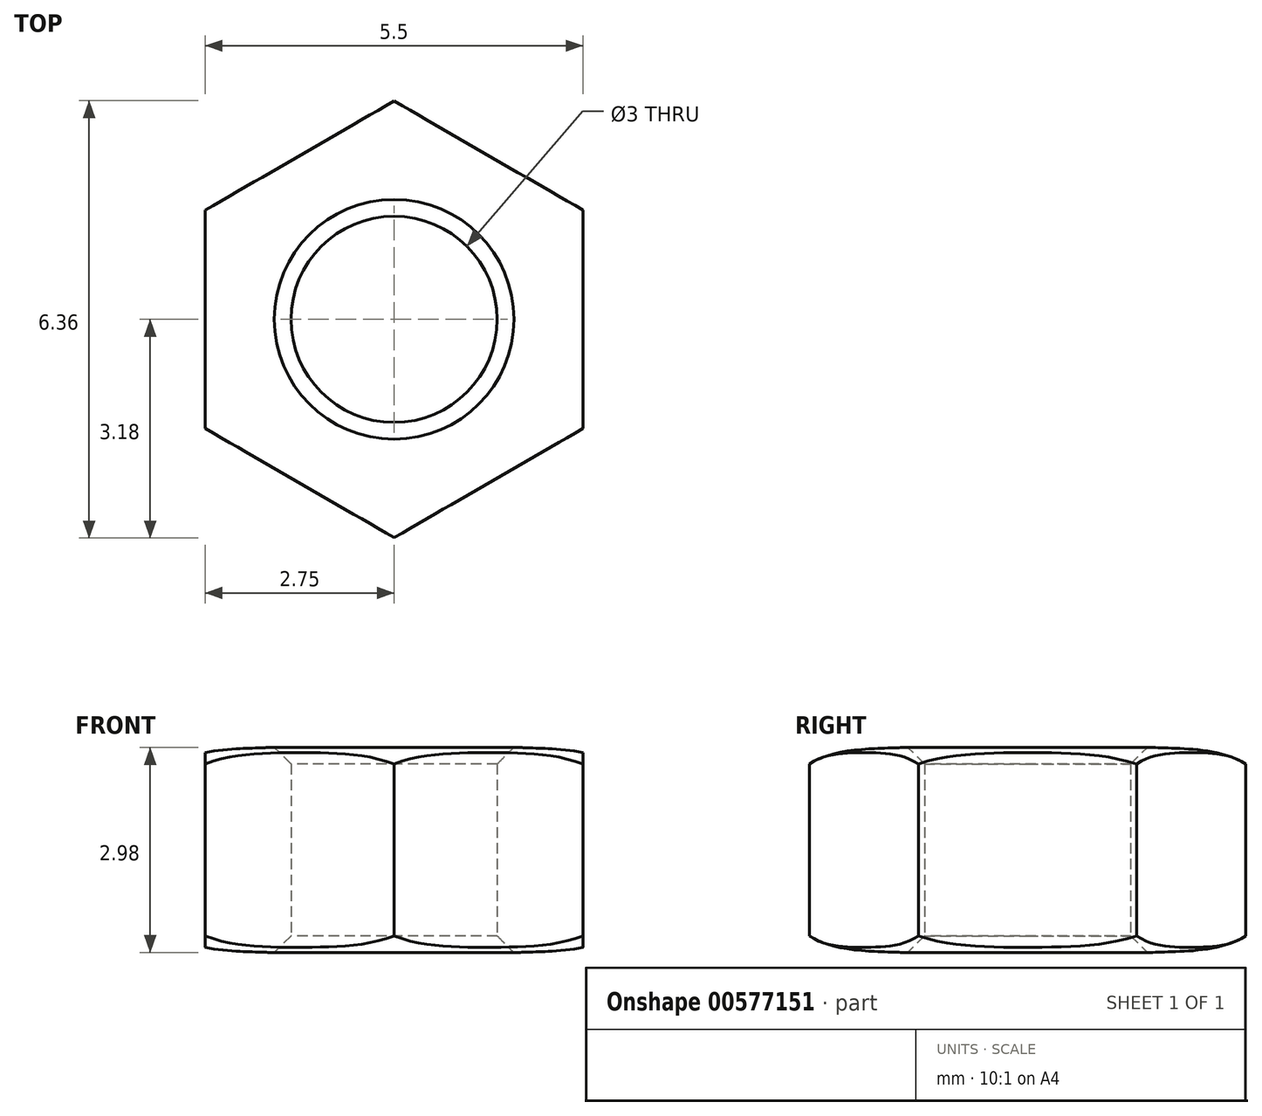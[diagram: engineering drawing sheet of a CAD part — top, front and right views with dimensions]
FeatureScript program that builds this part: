
annotation { "Feature Type Name" : "Feature", "Feature Type Description" : "" }
export const myFeature = defineFeature(function(context is Context, id is Id, definition is map)
    precondition{}
    {
        {
            var Q0;
            Q0=qCreatedBy(makeId("Top.planeOp"),FACE);
            var sketch = newSketch(context, id + "F0", { "sketchPlane" : qUnion([Q0])});
            skCircle(sketch, "E0.cCircle", {"center": v(0, 0) * mm, "radius": 2.75 * mm, "construction": true});
            skLineSegment(sketch, "E0.0", {"start": v(2.75, 1.59) * mm, "end": v(2.75, -1.59) * mm});
            skLineSegment(sketch, "E0.1", {"start": v(2.75, -1.59) * mm, "end": v(0, -3.18) * mm});
            skLineSegment(sketch, "E0.2", {"start": v(0, -3.18) * mm, "end": v(-2.75, -1.59) * mm});
            skLineSegment(sketch, "E0.3", {"start": v(-2.75, -1.59) * mm, "end": v(-2.75, 1.59) * mm});
            skLineSegment(sketch, "E0.4", {"start": v(-2.75, 1.59) * mm, "end": v(0, 3.18) * mm});
            skLineSegment(sketch, "E0.5", {"start": v(0, 3.18) * mm, "end": v(2.75, 1.59) * mm});
            skPoint(sketch, "E0.0.midPoint", {"position": v(2.75, 0) * mm});
            skCircle(sketch, "E1", {"center": v(0, 0) * mm, "radius": 1.5 * mm});
            skSolve(sketch);
        }
        {
            var Q0;
            Q0=qSketchRegion(id+"F0",true);
            extrude(context, id + "F1", {"entities" : qUnion([Q0]), "endBound" : BoundingType.SYMMETRIC, "depth" : 3 * mm});
        }
        {
            var Q0;
            Q0=makeQuery(id+"F1.opExtrude","CAP_EDGE",EDGE,{"disambiguationData":[OSD([sQuery(id+"F0.wireOp",EDGE,"E1")])],"isStart":false});
            chamfer(context, id + "F2", {"entities" : qUnion([Q0]), "width" : 0.25 * mm, "tangentPropagation" : true});
        }
        {
            var Q0;
            Q0=makeQuery(id+"F1.opExtrude","CAP_EDGE",EDGE,{"disambiguationData":[OSD([sQuery(id+"F0.wireOp",EDGE,"E1")])],"isStart":true});
            chamfer(context, id + "F3", {"entities" : qUnion([Q0]), "width" : 0.25 * mm, "tangentPropagation" : true});
        }
        {
            var Q0;
            Q0=qCreatedBy(makeId("Right.planeOp"),FACE);
            var sketch = newSketch(context, id + "F4", { "sketchPlane" : qUnion([Q0])});
            skFitSpline(sketch, "E2", {"points": [v(0, 1.5) * mm, v(2, 1.48) * mm, v(3.47, 0.9) * mm], "startDerivative": vector(8.87, 0.07) * mm, "endDerivative": vector(1.26, -3.57) * mm});
            skFitSpline(sketch, "E3.MirrorCS", {"points": [v(0, -1.5) * mm, v(2, -1.48) * mm, v(3.47, -0.9) * mm], "startDerivative": vector(8.87, -0.07) * mm, "endDerivative": vector(1.26, 3.57) * mm});
            skLineSegment(sketch, "E4", {"start": v(3.47, 0.9) * mm, "end": v(3.47, -0.9) * mm});
            skLineSegment(sketch, "E5", {"start": v(0, 1.5) * mm, "end": v(0, 1.9) * mm});
            skLineSegment(sketch, "E6", {"start": v(0, 1.9) * mm, "end": v(4.12, 1.9) * mm});
            skLineSegment(sketch, "E7", {"start": v(4.12, 1.9) * mm, "end": v(4.12, -1.85) * mm});
            skLineSegment(sketch, "E8", {"start": v(4.12, -1.85) * mm, "end": v(0, -1.85) * mm});
            skLineSegment(sketch, "E9", {"start": v(0, -1.85) * mm, "end": v(0, -1.5) * mm});
            skSolve(sketch);
        }
        {
            var Q0;
            Q0=qSketchRegion(id+"F4",true);
            var Q1;
            Q1=makeQuery(id+"F1.opExtrude","SWEPT_FACE",FACE,{"disambiguationData":[OSD([sQuery(id+"F0.wireOp",EDGE,"E1")])]});
            revolve(context, id + "F5", {"operationType" : NewBodyOperationType.REMOVE, "entities" : qUnion([Q0]), "axis" : qUnion([Q1]), "revolveType" : RevolveType.FULL, "oppositeDirection" : true});
        }
    });
